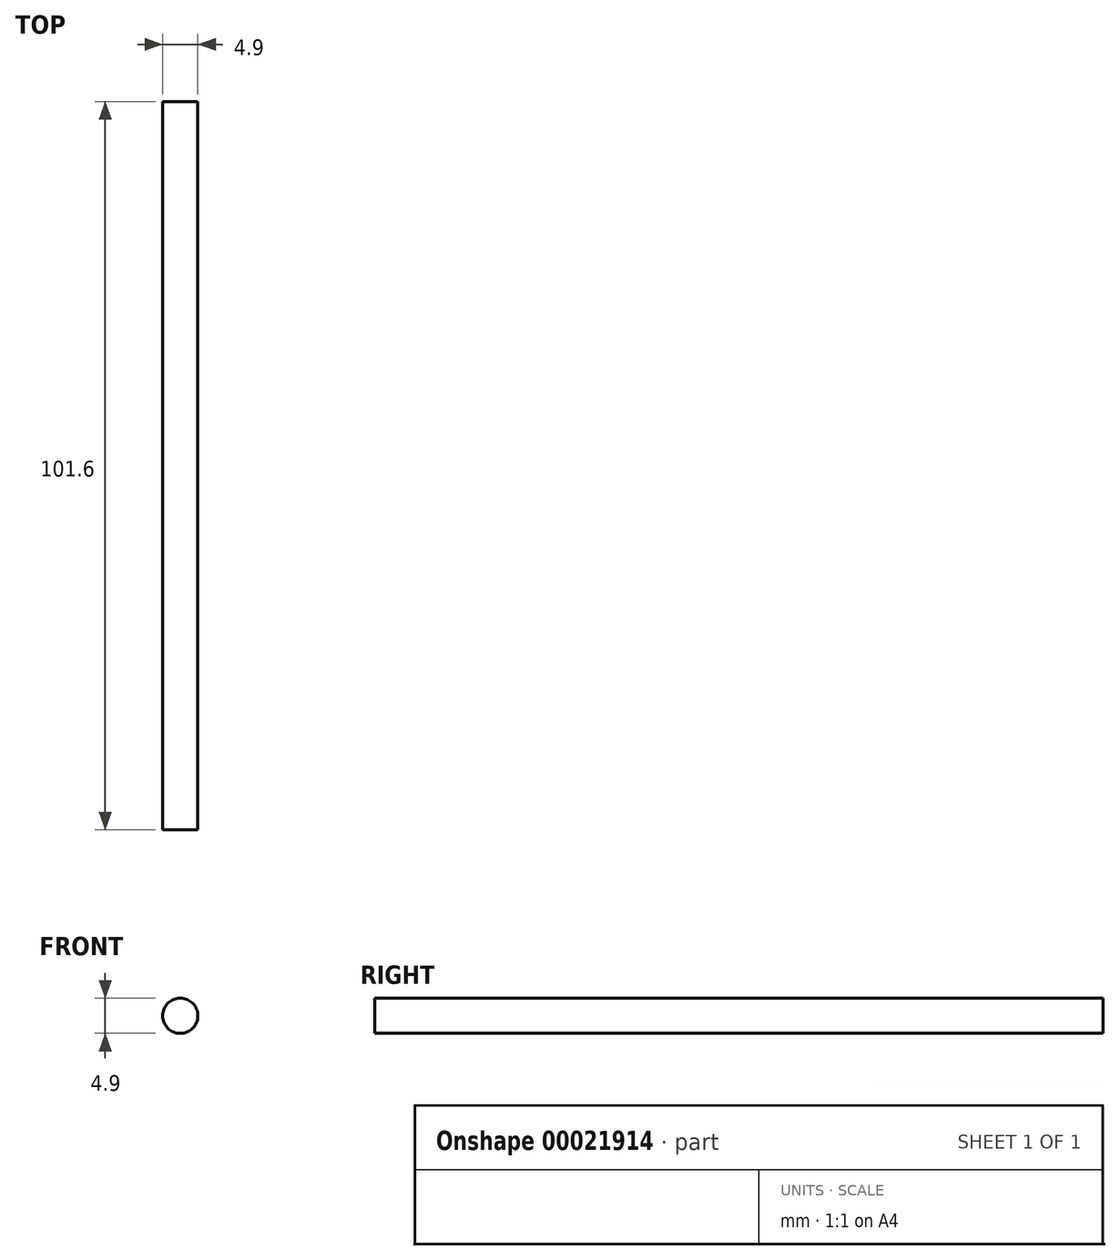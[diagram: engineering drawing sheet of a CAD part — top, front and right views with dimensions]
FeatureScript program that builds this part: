
annotation { "Feature Type Name" : "Feature", "Feature Type Description" : "" }
export const myFeature = defineFeature(function(context is Context, id is Id, definition is map)
    precondition{}
    {
        {
            var Q0;
            Q0=qCreatedBy(makeId("Front.planeOp"),FACE);
            var sketch = newSketch(context, id + "F0", { "sketchPlane" : qUnion([Q0])});
            skCircle(sketch, "E0", {"center": v(0, 0) * mm, "radius": 2.45 * mm});
            skSolve(sketch);
        }
        {
            var Q0;
            Q0 = qSketchRegion(id + "F0", true);
            extrude(context, id + "F1", {"entities" : qUnion([Q0]), "depth" : 101.6 * mm});
        }
    });
